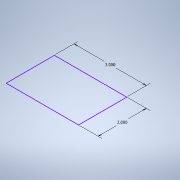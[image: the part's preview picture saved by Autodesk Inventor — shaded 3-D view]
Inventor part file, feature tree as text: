
AUTODESK INVENTOR PART (.ipt)
format: ipt  version: 2020 (Build 240168000, 168)  size: 181,248 bytes
history: native  units: in
note: dims shown in document units (in); Inventor stores cm internally (conversion verified against a paired STEP export)
features: sketch x4, extrude x3
ambient origin geometry x8: Origin, YZ Plane, XZ Plane, XY Plane, X Axis, Y Axis, Z Axis, Center Point
bodies: Body1 (feature_tree)
feature tree (7):
  extrude  "Extrusion2"  Depth=0.75in
  extrude  "Extrusion3"  Depth=0.15in TaperAngle=0.0deg
  extrude  "Extrusion4"  Depth=0.15in
  sketch  "Sketch6"  dims[d23=0.15in d24=0.0in d25=0.315in d26=0.1181in d27=0.15in d28=0.0in]
  sketch  "Sketch3"  dims[d9=1.75in d10=0.75in]
  sketch  "Sketch4"  dims[d11=1.4272in d12=0.1772in d13=0.1772in d14=1.1811in d15=0.4724in]
  sketch  "Sketch5"  dims[d16=1.4272in d17=0.1772in d18=0.1772in d19=1.1811in d20=0.4724in d21=0.15in d22=0.0in]
